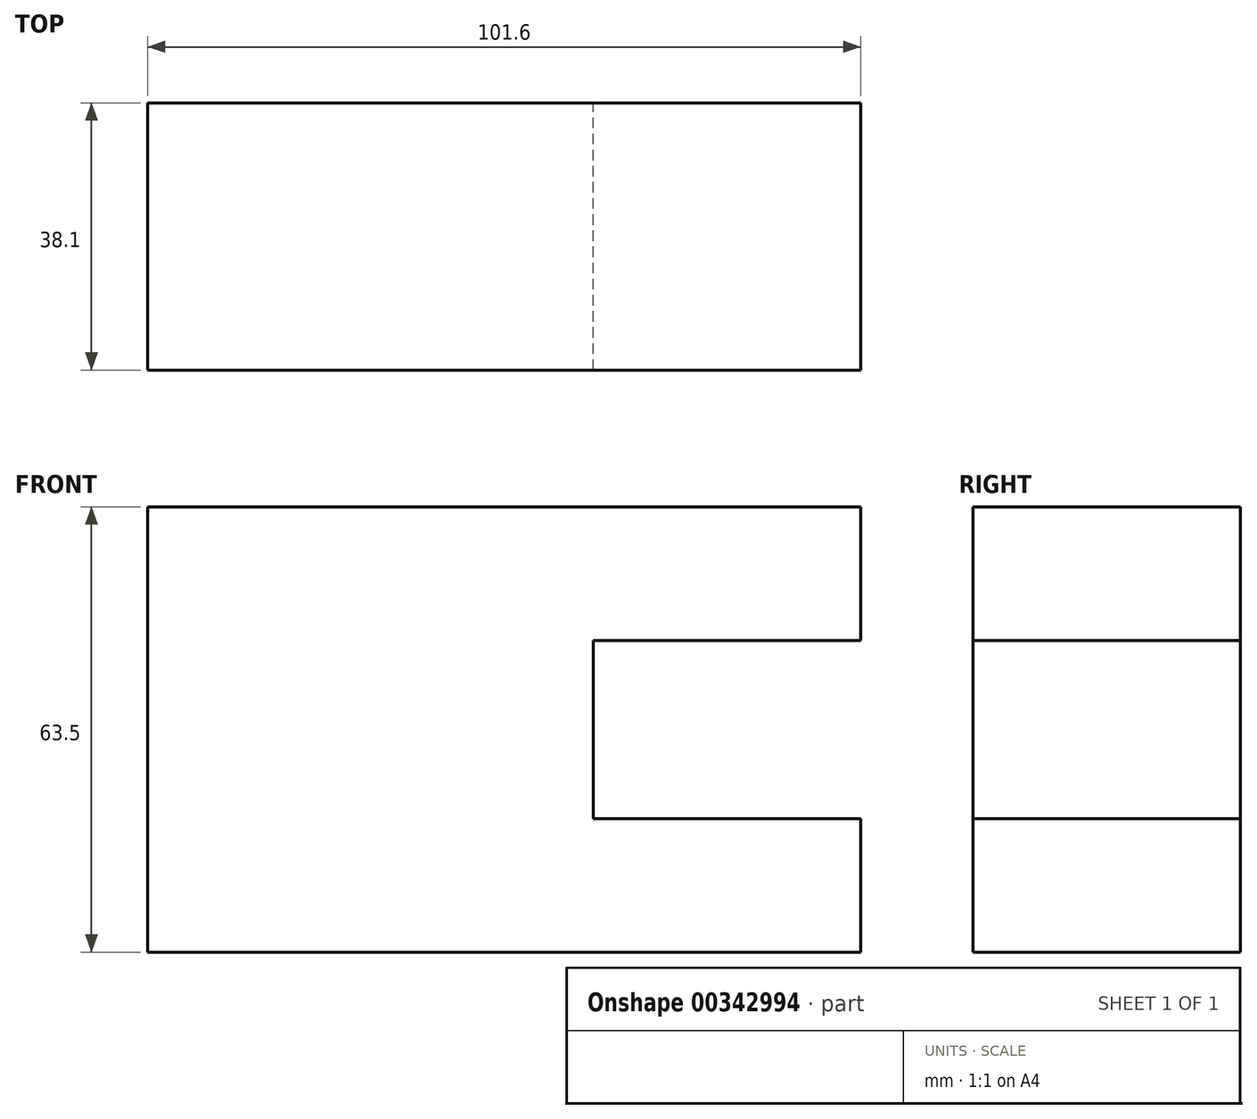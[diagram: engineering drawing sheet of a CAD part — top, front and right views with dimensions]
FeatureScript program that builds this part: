
annotation { "Feature Type Name" : "Feature", "Feature Type Description" : "" }
export const myFeature = defineFeature(function(context is Context, id is Id, definition is map)
    precondition{}
    {
        {
            var Q0;
            Q0=qCreatedBy(makeId("Front.planeOp"),FACE);
            var sketch = newSketch(context, id + "F0", { "sketchPlane" : qUnion([Q0])});
            skLineSegment(sketch, "E0", {"start": v(-63.5, -38.1) * mm, "end": v(38.1, -38.1) * mm});
            skLineSegment(sketch, "E1", {"start": v(-63.5, -38.1) * mm, "end": v(-63.5, 25.4) * mm});
            skLineSegment(sketch, "E2", {"start": v(38.1, -38.1) * mm, "end": v(38.1, -19.05) * mm});
            skLineSegment(sketch, "E3", {"start": v(-63.5, 25.4) * mm, "end": v(38.1, 25.4) * mm});
            skLineSegment(sketch, "E4", {"start": v(38.1, -19.05) * mm, "end": v(0, -19.05) * mm});
            skLineSegment(sketch, "E5", {"start": v(38.1, 25.4) * mm, "end": v(38.1, 6.35) * mm});
            skLineSegment(sketch, "E6", {"start": v(38.1, 6.35) * mm, "end": v(0, 6.35) * mm});
            skLineSegment(sketch, "E7", {"start": v(0, 6.35) * mm, "end": v(0, -19.05) * mm});
            skSolve(sketch);
        }
        {
            var Q0;
            Q0=makeQuery(id+"F0.imprint","IMPRINT",FACE,{"disambiguationData":[TD([[makeQuery(id+"F0.imprint","IMPRINT",EDGE,{"derivedFrom":sQuery(id+"F0.wireOp",EDGE,"E0")}),1.0]])]});
            extrude(context, id + "F1", {"entities" : qUnion([Q0]), "depth" : 38.1 * mm});
        }
    });
